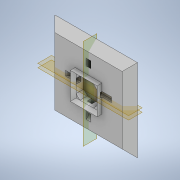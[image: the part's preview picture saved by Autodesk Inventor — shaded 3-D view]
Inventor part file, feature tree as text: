
AUTODESK INVENTOR PART (.ipt)
format: ipt  version: 2021 (Build 250183000, 183)  size: 238,080 bytes
history: native  units: in
note: dims shown in document units (in); Inventor stores cm internally (conversion verified against a paired STEP export)
features: sketch x8, projected_geometry x8, extrude x4, plane x4, sweep x3, chamfer x2
ambient origin geometry x8: Origin, YZ Plane, XZ Plane, XY Plane, X Axis, Y Axis, Z Axis, Center Point
bodies: Solid1 (feature_tree)
feature tree (29):
  extrude  "Extrusion1"  Depth=0.1575in
  chamfer  "Chamfer1"  Distance=0.1575in
  extrude  "Extrusion2"  Depth=0.1181in TaperAngle=0.0deg
  plane  "Work Plane4"
  extrude  "Extrusion7"  Depth=0.0984in TaperAngle=0.0deg
  chamfer  "Chamfer6"  Distance=0.0591in Angle=45.0deg
  extrude  "Extrusion8"  Depth=0.0197in
  plane  "Work Plane6"
  plane  "Work Plane7"
  sketch  "Sketch17"  dims[d105=1.6929in d106=1.6929in]
  sketch  "Sketch18"  dims[d107=0.0394in d108=0.0in d109=0.0492in]
  sweep  "Sweep4"
  sweep  "Sweep5"
  plane  "Work Plane8"
  sweep  "Sweep6"
  sketch  "Sketch1"  dims[d0=1.7323in d1=1.7323in d2=0.1575in d3=0.0in]
  sketch  "Sketch2"  dims[d4=0.1575in d5=0.0787in d6=45.0deg d8=0.1181in d9=0.0in]
  sketch  "Sketch15"  dims[d86=0.0787in d98=0.0984in d99=0.0in d100=0.0591in d101=0.0787in d102=45.0deg]
  projected_geometry  "Projected Loop6"
  sketch  "Sketch16"  dims[d103=0.0197in d104=0.0197in]
  projected_geometry  "Projected Loop7"
  projected_geometry  "Projected Loop8"
  projected_geometry  "Projected Loop9"
  projected_geometry  "Projected Loop10"
  projected_geometry  "Projected Loop11"
  projected_geometry  "Projected Loop12"
  sketch  "Sketch19"  dims[d110=0.0984in d111=0.0984in]
  projected_geometry  "Projected Loop13"
  sketch  "Sketch20"  dims[d113=0.3937in d114=135.0deg d117=0.0in d118=0.0in d119=0.0in d120=0.0in d121=0.0787in d127=0.0492in d128=0.0984in d129=0.0984in d130=0.0492in d131=0.3937in d132=135.0deg d134=0.3937in d135=0.0in d136=0.0in]
